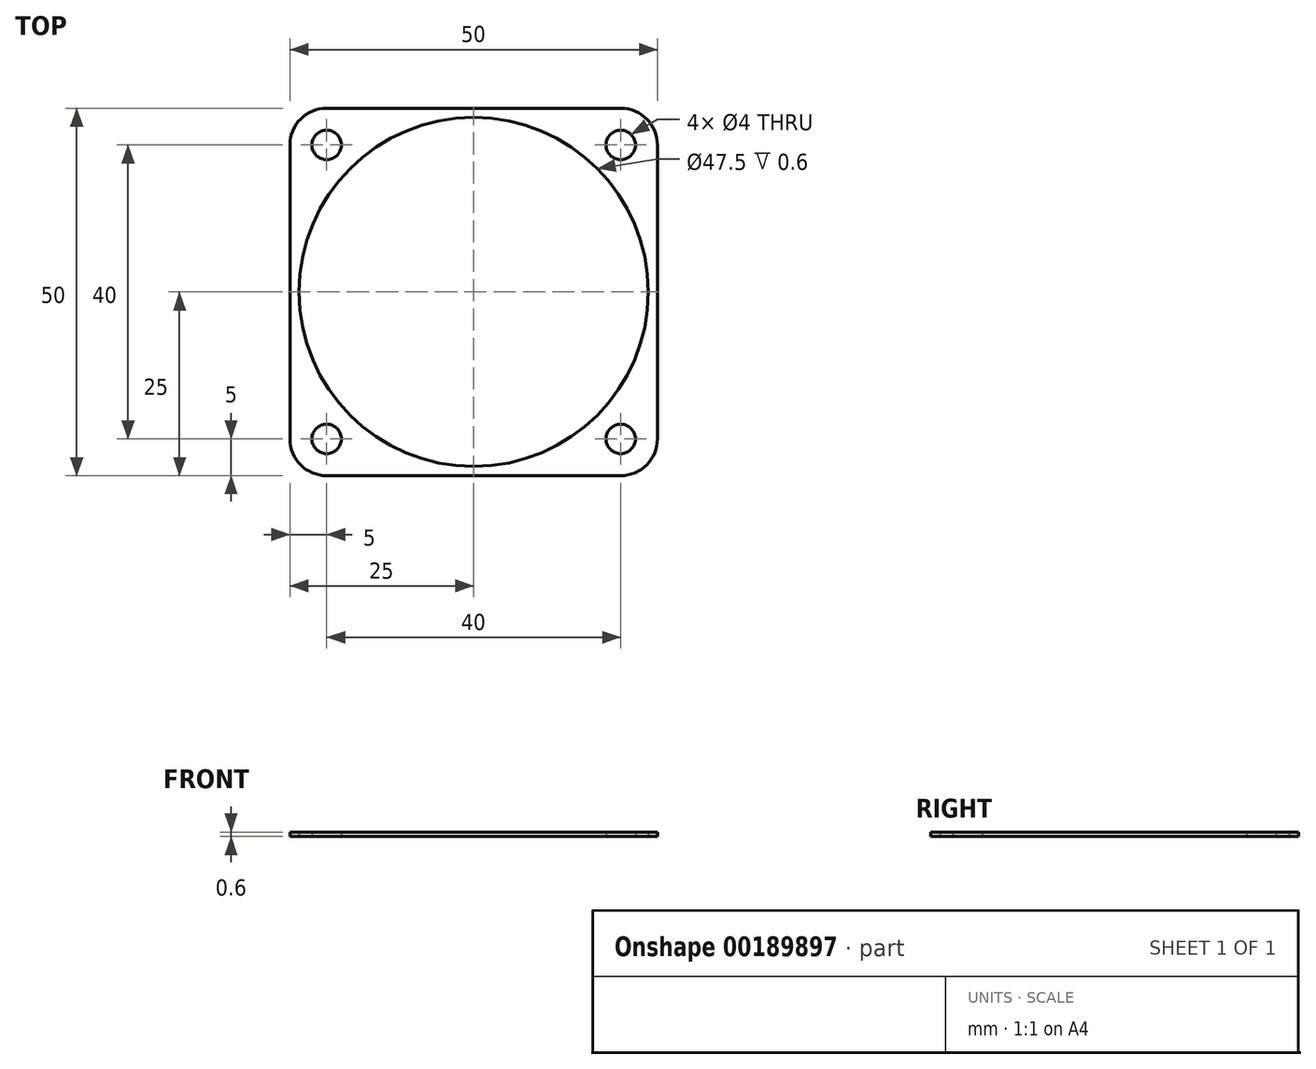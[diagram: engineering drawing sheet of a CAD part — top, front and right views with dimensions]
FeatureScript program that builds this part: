
annotation { "Feature Type Name" : "Feature", "Feature Type Description" : "" }
export const myFeature = defineFeature(function(context is Context, id is Id, definition is map)
    precondition{}
    {
        {
            var Q0;
            Q0=qCreatedBy(makeId("Top.planeOp"),FACE);
            var sketch = newSketch(context, id + "F0", { "sketchPlane" : qUnion([Q0])});
            skLineSegment(sketch, "E0.bottom", {"start": v(-5, 0) * mm, "end": v(-45, 0) * mm});
            skLineSegment(sketch, "E0.top", {"start": v(-5, 50) * mm, "end": v(-45, 50) * mm});
            skLineSegment(sketch, "E0.left", {"start": v(0, 5) * mm, "end": v(0, 45) * mm});
            skLineSegment(sketch, "E0.right", {"start": v(-50, 5) * mm, "end": v(-50, 45) * mm});
            skCircle(sketch, "E1", {"center": v(-45, 45) * mm, "radius": 2 * mm});
            skCircle(sketch, "E2", {"center": v(-5, 5) * mm, "radius": 2 * mm});
            skCircle(sketch, "E3", {"center": v(-45, 5) * mm, "radius": 2 * mm});
            skCircle(sketch, "E4", {"center": v(-5, 45) * mm, "radius": 2 * mm});
            skCircle(sketch, "E5", {"center": v(-25, 25) * mm, "radius": 23.75 * mm});
            skLineSegment(sketch, "E6", {"start": v(-50, 25) * mm, "end": v(-1.25, 25) * mm, "construction": true});
            skPoint(sketch, "E6.endSnap0", {"position": v(0, 25) * mm});
            skLineSegment(sketch, "E7", {"start": v(-25, 50) * mm, "end": v(-25, 0) * mm, "construction": true});
            skPoint(sketch, "E8.visualSharp", {"position": v(-50, 50) * mm});
            skArc(sketch, "E8.filletArc", {"start": v(-45, 50) * mm, "mid": v(-48.54, 48.54) * mm, "end": v(-50, 45) * mm});
            skPoint(sketch, "E9.visualSharp", {"position": v(-50, 0) * mm});
            skArc(sketch, "E9.filletArc", {"start": v(-50, 5) * mm, "mid": v(-48.54, 1.46) * mm, "end": v(-45, 0) * mm});
            skPoint(sketch, "E10.visualSharp", {"position": v(0, 0) * mm});
            skArc(sketch, "E10.filletArc", {"start": v(-5, 0) * mm, "mid": v(-1.46, 1.46) * mm, "end": v(0, 5) * mm});
            skPoint(sketch, "E11.visualSharp", {"position": v(0, 50) * mm});
            skArc(sketch, "E11.filletArc", {"start": v(0, 45) * mm, "mid": v(-1.46, 48.54) * mm, "end": v(-5, 50) * mm});
            skSolve(sketch);
        }
        {
            var Q0;
            Q0=makeQuery(id+"F0.imprint","IMPRINT",FACE,{"disambiguationData":[TD([[makeQuery(id+"F0.imprint","IMPRINT",EDGE,{"derivedFrom":sQuery(id+"F0.wireOp",EDGE,"E0.bottom")}),-1.0]])]});
            extrude(context, id + "F1", {"entities" : qUnion([Q0]), "depth" : .6 * mm});
        }
    });
